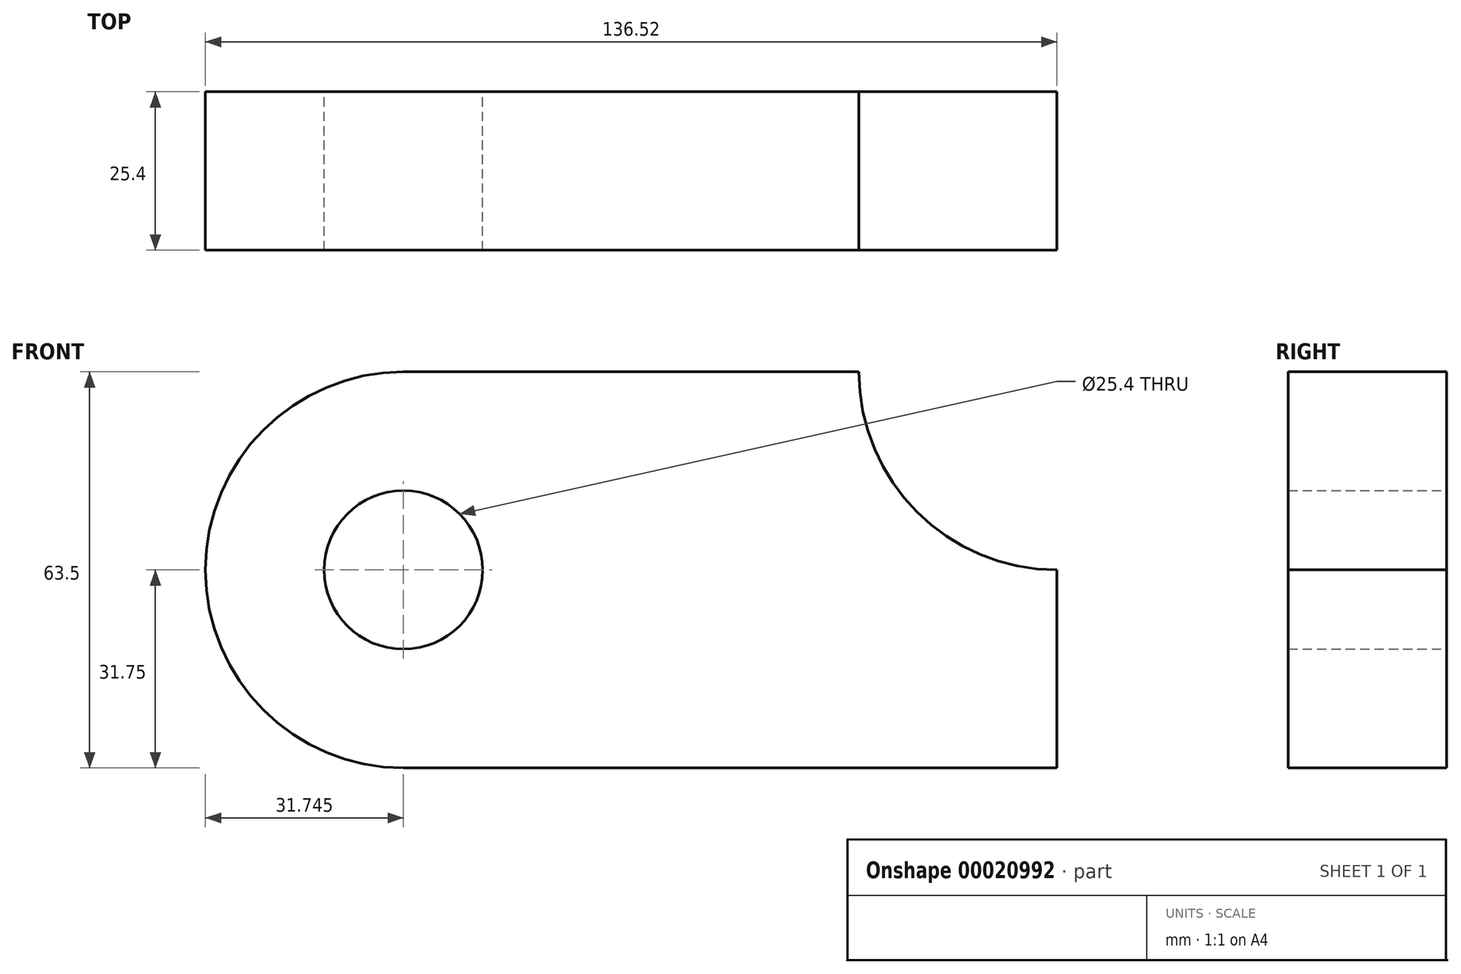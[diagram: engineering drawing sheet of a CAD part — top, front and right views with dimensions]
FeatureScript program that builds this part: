
annotation { "Feature Type Name" : "Feature", "Feature Type Description" : "" }
export const myFeature = defineFeature(function(context is Context, id is Id, definition is map)
    precondition{}
    {
        {
            var Q0;
            Q0=qCreatedBy(makeId("Front.planeOp"),FACE);
            var sketch = newSketch(context, id + "F0", { "sketchPlane" : qUnion([Q0])});
            skLineSegment(sketch, "E0.bottom", {"start": v(0, 0) * mm, "end": v(-104.77, 0) * mm});
            skLineSegment(sketch, "E0.top", {"start": v(0, 63.5) * mm, "end": v(-104.78, 63.5) * mm});
            skLineSegment(sketch, "E0.left", {"start": v(0, 0) * mm, "end": v(0, 63.5) * mm});
            skLineSegment(sketch, "E0.right", {"start": v(-104.77, 0) * mm, "end": v(-104.77, 63.5) * mm});
            skPoint(sketch, "E1.center.orphan", {"position": v(-104.78, 31.75) * mm});
            skCircle(sketch, "E2", {"center": v(-104.78, 31.75) * mm, "radius": 31.75 * mm});
            skCircle(sketch, "E3", {"center": v(-104.78, 31.75) * mm, "radius": 12.7 * mm});
            skCircle(sketch, "E4", {"center": v(0, 63.5) * mm, "radius": 31.75 * mm});
            skSolve(sketch);
        }
        {
            var Q0;
            {var subQ0=sQuery(id+"F0.wireOp",EDGE,"E3");var subQ1=sQuery(id+"F0.wireOp",EDGE,"E0.right");var subQ3=makeQuery(id+"F0.imprint","INTERSECT",VERTEX,{"disambiguationData":[OD(0.0)],"derivedFrom":[subQ1,subQ0]});Q0=makeQuery(id+"F0.imprint","IMPRINT",FACE,{"disambiguationData":[TD([[makeQuery(id+"F0.imprint","IMPRINT",EDGE,{"disambiguationData":[TD([[subQ3,1.0]])],"derivedFrom":subQ0}),-1.0]])]});}
            var Q1;
            {var subQ0=sQuery(id+"F0.wireOp",EDGE,"E3");var subQ1=sQuery(id+"F0.wireOp",EDGE,"E0.right");var subQ3=makeQuery(id+"F0.imprint","INTERSECT",VERTEX,{"disambiguationData":[OD(0.0)],"derivedFrom":[subQ1,subQ0]});Q1=makeQuery(id+"F0.imprint","IMPRINT",FACE,{"disambiguationData":[TD([[makeQuery(id+"F0.imprint","IMPRINT",EDGE,{"disambiguationData":[TD([[subQ3,-1.0]])],"derivedFrom":subQ0}),-1.0]])]});}
            var Q2;
            {var subQ4=sQuery(id+"F0.wireOp",EDGE,"E0.bottom");Q2=makeQuery(id+"F0.imprint","IMPRINT",FACE,{"disambiguationData":[TD([[makeQuery(id+"F0.imprint","IMPRINT",EDGE,{"derivedFrom":subQ4}),-1.0]])]});}
            extrude(context, id + "F1", {"entities" : qUnion([Q0, Q1, Q2]), "depth" : 25.4 * mm});
        }
    });
